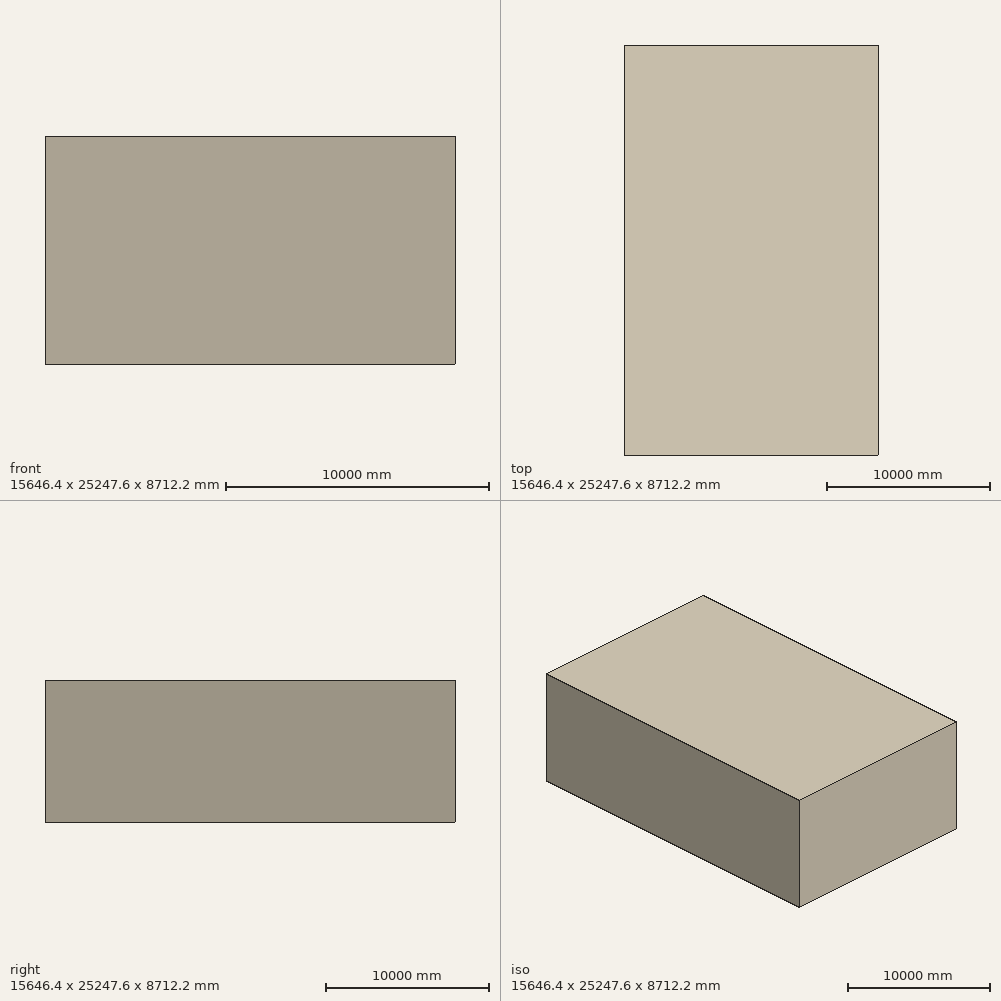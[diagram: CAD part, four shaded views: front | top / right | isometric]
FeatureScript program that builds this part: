
annotation { "Feature Type Name" : "Feature", "Feature Type Description" : "" }
export const myFeature = defineFeature(function(context is Context, id is Id, definition is map)
    precondition{}
    {
        {
            var Q0;
            Q0=qCreatedBy(makeId("Top.planeOp"),FACE);
            var sketch = newSketch(context, id + "F0", { "sketchPlane" : qUnion([Q0])});
            skLineSegment(sketch, "E0.bottom", {"start": v(0, 0) * mm, "end": v(15646.4, 0) * mm});
            skLineSegment(sketch, "E0.top", {"start": v(0, 25247.6) * mm, "end": v(15646.4, 25247.6) * mm});
            skLineSegment(sketch, "E0.left", {"start": v(0, 0) * mm, "end": v(0, 25247.6) * mm});
            skLineSegment(sketch, "E0.right", {"start": v(15646.4, 0) * mm, "end": v(15646.4, 25247.6) * mm});
            skSolve(sketch);
        }
        {
            var Q0;
            Q0 = qSketchRegion(id + "F0", true);
            extrude(context, id + "F1", {"entities" : qUnion([Q0]), "depth" : 8712.2 * mm, "offsetDistance" : 25.4 * mm});
        }
    });
